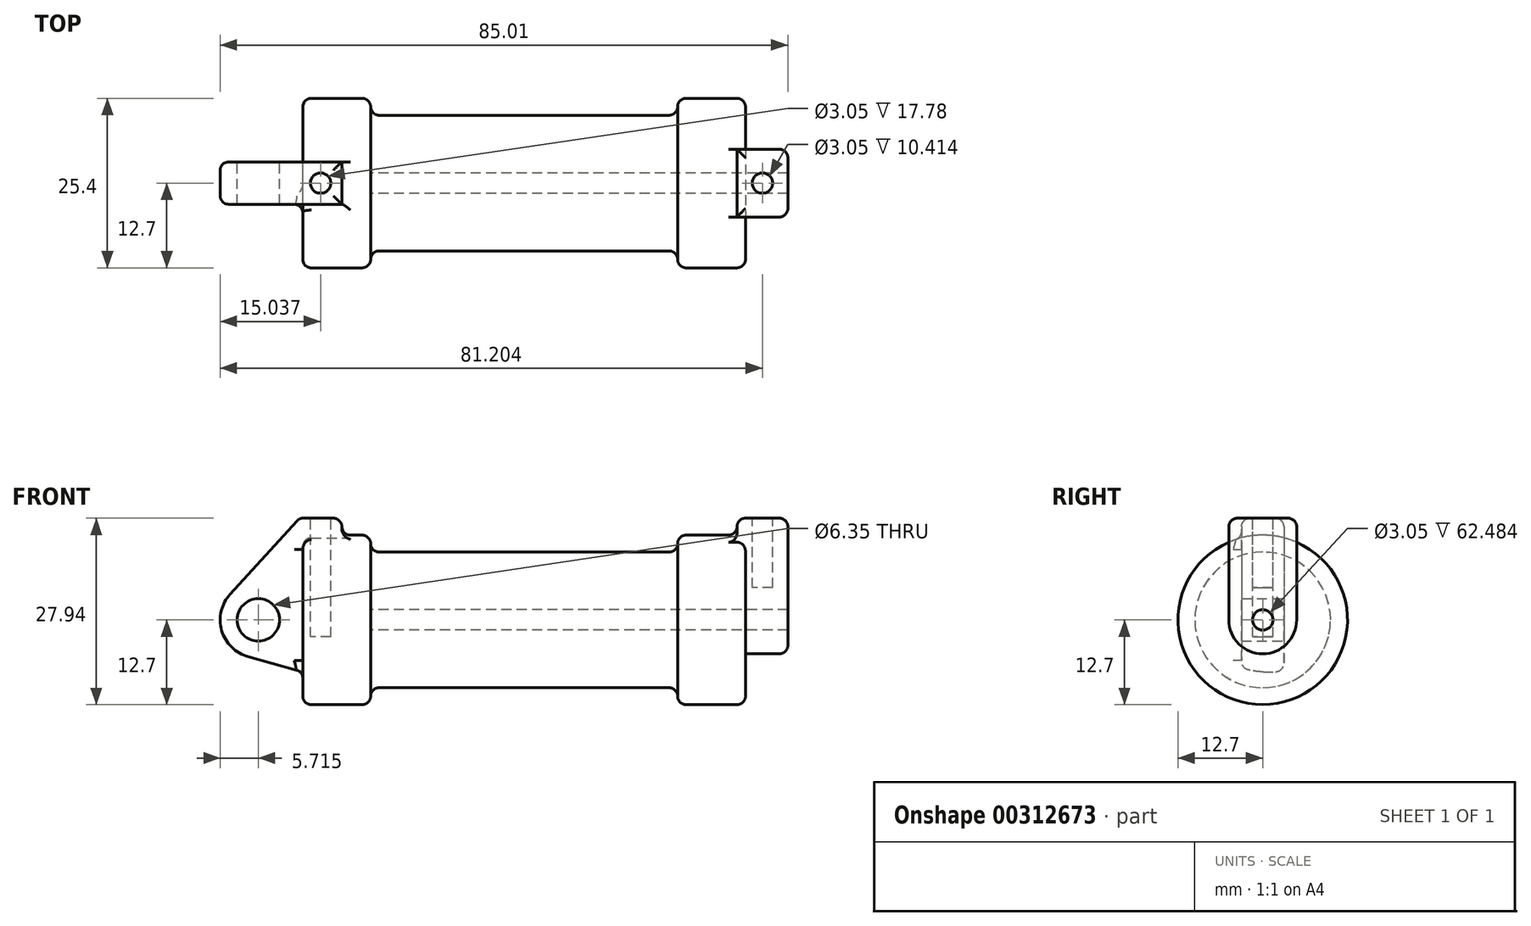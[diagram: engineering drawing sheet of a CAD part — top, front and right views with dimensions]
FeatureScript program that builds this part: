
annotation { "Feature Type Name" : "Feature", "Feature Type Description" : "" }
export const myFeature = defineFeature(function(context is Context, id is Id, definition is map)
    precondition{}
    {
        {
            var Q0;
            Q0=qCreatedBy(makeId("Front.planeOp"),FACE);
            var sketch = newSketch(context, id + "F0", { "sketchPlane" : qUnion([Q0])});
            skLineSegment(sketch, "E0", {"start": v(0, 0) * mm, "end": v(0, 12.7) * mm});
            skLineSegment(sketch, "E1", {"start": v(0, 12.7) * mm, "end": v(10.16, 12.7) * mm});
            skLineSegment(sketch, "E2", {"start": v(10.16, 12.7) * mm, "end": v(10.16, 10.16) * mm});
            skLineSegment(sketch, "E3", {"start": v(10.16, 10.16) * mm, "end": v(56.13, 10.16) * mm});
            skLineSegment(sketch, "E4", {"start": v(56.13, 10.16) * mm, "end": v(56.13, 12.7) * mm});
            skLineSegment(sketch, "E5", {"start": v(56.13, 12.7) * mm, "end": v(66.3, 12.7) * mm});
            skLineSegment(sketch, "E6", {"start": v(66.3, 12.7) * mm, "end": v(66.3, 0) * mm});
            skLineSegment(sketch, "E7", {"start": v(66.3, 0) * mm, "end": v(0, 0) * mm});
            skLineSegment(sketch, "E8", {"start": v(5.84, 15.24) * mm, "end": v(-0.5, 15.24) * mm});
            skLineSegment(sketch, "E9", {"start": v(-0.5, 15.24) * mm, "end": v(-10.88, 3.85) * mm});
            skLineSegment(sketch, "E10", {"start": v(0, 0) * mm, "end": v(-6.65, 0) * mm});
            skCircle(sketch, "E11", {"center": v(-6.65, 0) * mm, "radius": 5.72 * mm});
            skCircle(sketch, "E12", {"center": v(-6.65, 0) * mm, "radius": 3.18 * mm});
            skLineSegment(sketch, "E13", {"start": v(5.84, 15.24) * mm, "end": v(5.84, -9.4) * mm});
            skLineSegment(sketch, "E14", {"start": v(5.84, -9.4) * mm, "end": v(-8.18, -5.5) * mm});
            skSolve(sketch);
        }
        {
            var Q0;
            {var subQ0=sQuery(id+"F0.wireOp",EDGE,"E2");Q0=makeQuery(id+"F0.imprint","IMPRINT",FACE,{"disambiguationData":[TD([[makeQuery(id+"F0.imprint","IMPRINT",EDGE,{"derivedFrom":subQ0}),-1.0]])]});}
            var Q1;
            {var subQ0=sQuery(id+"F0.wireOp",EDGE,"E0");Q1=makeQuery(id+"F0.imprint","IMPRINT",FACE,{"disambiguationData":[TD([[makeQuery(id+"F0.imprint","IMPRINT",EDGE,{"derivedFrom":subQ0}),-1.0]])]});}
            var Q2;
            Q2=sQuery(id+"F0.wireOp",EDGE,"E7");
            revolve(context, id + "F1", {"entities" : qUnion([Q0, Q1]), "axis" : qUnion([Q2]), "revolveType" : RevolveType.FULL});
        }
        {
            var Q0;
            {var subQ0=sQuery(id+"F0.wireOp",EDGE,"E0");Q0=makeQuery(id+"F0.imprint","IMPRINT",FACE,{"disambiguationData":[TD([[makeQuery(id+"F0.imprint","IMPRINT",EDGE,{"derivedFrom":subQ0}),-1.0]])]});}
            var Q1;
            {var subQ1=sQuery(id+"F0.wireOp",EDGE,"E0");Q1=makeQuery(id+"F0.imprint","IMPRINT",FACE,{"disambiguationData":[TD([[makeQuery(id+"F0.imprint","IMPRINT",EDGE,{"derivedFrom":subQ1}),1.0]])]});}
            var Q2;
            {var subQ5=sQuery(id+"F0.wireOp",EDGE,"E12");Q2=makeQuery(id+"F0.imprint","IMPRINT",FACE,{"disambiguationData":[TD([[makeQuery(id+"F0.imprint","IMPRINT",EDGE,{"derivedFrom":subQ5}),-1.0]])]});}
            var Q3;
            {var subQ0=sQuery(id+"F0.wireOp",EDGE,"E14");Q3=makeQuery(id+"F0.imprint","IMPRINT",FACE,{"disambiguationData":[TD([[makeQuery(id+"F0.imprint","IMPRINT",EDGE,{"derivedFrom":subQ0}),-1.0]])]});}
            extrude(context, id + "F2", {"entities" : qUnion([Q0, Q1, Q2, Q3]), "operationType" : NewBodyOperationType.ADD, "endBound" : BoundingType.SYMMETRIC, "depth" : 6.35 * mm});
        }
        {
            var Q0;
            Q0=makeQuery(id+"F1.opRevolve","SWEPT_FACE",FACE,{"disambiguationData":[OSD([sQuery(id+"F0.wireOp",EDGE,"E6")])]});
            var sketch = newSketch(context, id + "F3", { "sketchPlane" : qUnion([Q0])});
            skCircle(sketch, "E15", {"center": v(0, 0) * mm, "radius": 1.52 * mm});
            skCircle(sketch, "E16", {"center": v(0, 0) * mm, "radius": 5.08 * mm});
            skLineSegment(sketch, "E17", {"start": v(5.08, 0) * mm, "end": v(5.08, 15.24) * mm});
            skLineSegment(sketch, "E18", {"start": v(5.08, 15.24) * mm, "end": v(-5.08, 15.24) * mm});
            skLineSegment(sketch, "E19", {"start": v(-5.08, 15.24) * mm, "end": v(-5.08, 0) * mm});
            skSolve(sketch);
        }
        {
            var Q0;
            {var subQ0=sQuery(id+"F3.wireOp",EDGE,"E18");Q0=makeQuery(id+"F3.imprint","IMPRINT",FACE,{"disambiguationData":[TD([[makeQuery(id+"F3.imprint","IMPRINT",EDGE,{"derivedFrom":subQ0}),1.0]])]});}
            var Q1;
            {var subQ0=sQuery(id+"F3.wireOp",EDGE,"E17");var subQ1=sQuery(id+"F3.wireOp",EDGE,"E16");var subQ2=makeQuery(id+"F3.imprint","INTERSECT",VERTEX,{"derivedFrom":[subQ1,subQ0]});Q1=makeQuery(id+"F3.imprint","IMPRINT",FACE,{"disambiguationData":[TD([[makeQuery(id+"F3.imprint","IMPRINT",EDGE,{"disambiguationData":[TD([[subQ2,-1.0]])],"derivedFrom":subQ1}),-1.0]])]});}
            var Q2;
            Q2=makeQuery(id+"F3.imprint","IMPRINT",FACE,{"disambiguationData":[TD([[makeQuery(id+"F3.imprint","IMPRINT",EDGE,{"derivedFrom":sQuery(id+"F3.wireOp",EDGE,"E15")}),-1.0]])]});
            extrude(context, id + "F4", {"entities" : qUnion([Q0, Q1, Q2]), "operationType" : NewBodyOperationType.ADD, "depth" : 6.35 * mm});
        }
        {
            var Q0;
            {var subQ0=sQuery(id+"F3.wireOp",EDGE,"E18");Q0=makeQuery(id+"F3.imprint","IMPRINT",FACE,{"disambiguationData":[TD([[makeQuery(id+"F3.imprint","IMPRINT",EDGE,{"derivedFrom":subQ0}),1.0]])]});}
            var Q1;
            {var subQ0=sQuery(id+"F3.wireOp",EDGE,"E17");var subQ1=sQuery(id+"F3.wireOp",EDGE,"E16");var subQ2=makeQuery(id+"F3.imprint","INTERSECT",VERTEX,{"derivedFrom":[subQ1,subQ0]});Q1=makeQuery(id+"F3.imprint","IMPRINT",FACE,{"disambiguationData":[TD([[makeQuery(id+"F3.imprint","IMPRINT",EDGE,{"disambiguationData":[TD([[subQ2,-1.0]])],"derivedFrom":subQ1}),-1.0]])]});}
            var Q2;
            Q2=makeQuery(id+"F3.imprint","IMPRINT",FACE,{"disambiguationData":[TD([[makeQuery(id+"F3.imprint","IMPRINT",EDGE,{"derivedFrom":sQuery(id+"F3.wireOp",EDGE,"E15")}),-1.0]])]});
            extrude(context, id + "F5", {"entities" : qUnion([Q0, Q1, Q2]), "operationType" : NewBodyOperationType.ADD, "oppositeDirection" : true, "depth" : 1.27 * mm});
        }
        {
            var Q0;
            Q0=makeQuery(id+"F4.boolean.opBoolean","SPLIT",FACE,{"disambiguationData":[TD([makeQuery(id+"F4.opExtrude","SWEPT_FACE",FACE,{"disambiguationData":[OSD([sQuery(id+"F3.wireOp",EDGE,"E15")])]})])],"derivedFrom":makeQuery(id+"F1.opRevolve","SWEPT_FACE",FACE,{"disambiguationData":[OSD([sQuery(id+"F0.wireOp",EDGE,"E6")])]})});
            var Q1;
            Q1=makeQuery(id+"F1.opRevolve","SWEPT_FACE",FACE,{"disambiguationData":[OSD([sQuery(id+"F0.wireOp",EDGE,"E2")])]});
            extrude(context, id + "F6", {"entities" : qUnion([Q0]), "operationType" : NewBodyOperationType.REMOVE, "endBound" : BoundingType.UP_TO_SURFACE, "oppositeDirection" : true, "endBoundEntityFace" : qUnion([Q1]), "depth" : 25.4 * mm});
        }
        {
            var Q0;
            Q0=makeQuery(id+"F2.opExtrude","SWEPT_FACE",FACE,{"disambiguationData":[OSD([sQuery(id+"F0.wireOp",EDGE,"E8")])]});
            var sketch = newSketch(context, id + "F7", { "sketchPlane" : qUnion([Q0])});
            skCircle(sketch, "E20", {"center": v(2.67, 0) * mm, "radius": 1.52 * mm});
            skSolve(sketch);
        }
        {
            var Q0;
            Q0=makeQuery(id+"F7.imprint","IMPRINT",FACE,{"disambiguationData":[TD([[makeQuery(id+"F7.imprint","IMPRINT",EDGE,{"derivedFrom":sQuery(id+"F7.wireOp",EDGE,"E20")}),1.0]])]});
            extrude(context, id + "F8", {"entities" : qUnion([Q0]), "operationType" : NewBodyOperationType.REMOVE, "oppositeDirection" : true, "depth" : 17.78 * mm});
        }
        {
            var Q0;
            {var subQ0=sQuery(id+"F3.wireOp",EDGE,"E18");Q0=makeQuery(id+"F5.boolean.opBoolean","MERGE",FACE,{"derivedFrom":[makeQuery(id+"F4.opExtrude","SWEPT_FACE",FACE,{"disambiguationData":[OSD([subQ0])]}),makeQuery(id+"F5.opExtrude","SWEPT_FACE",FACE,{"disambiguationData":[OSD([subQ0])]})]});}
            var sketch = newSketch(context, id + "F9", { "sketchPlane" : qUnion([Q0])});
            skCircle(sketch, "E21", {"center": v(68.83, 0) * mm, "radius": 1.52 * mm});
            skSolve(sketch);
        }
        {
            var Q0;
            Q0=makeQuery(id+"F9.imprint","IMPRINT",FACE,{"disambiguationData":[TD([[makeQuery(id+"F9.imprint","IMPRINT",EDGE,{"derivedFrom":sQuery(id+"F9.wireOp",EDGE,"E21")}),1.0]])]});
            extrude(context, id + "F10", {"entities" : qUnion([Q0]), "operationType" : NewBodyOperationType.REMOVE, "oppositeDirection" : true, "depth" : 10.4 * mm});
        }
        {
            var Q0;
            Q0=makeQuery(id+"F1.opRevolve","SWEPT_EDGE",EDGE,{"disambiguationData":[OSD([sQuery(id+"F0.wireOp",EDGE,"E2"),sQuery(id+"F0.wireOp",EDGE,"E3")])]});
            var Q1;
            Q1=makeQuery(id+"F1.opRevolve","SWEPT_EDGE",EDGE,{"disambiguationData":[OSD([sQuery(id+"F0.wireOp",EDGE,"E1"),sQuery(id+"F0.wireOp",EDGE,"E2")])]});
            var Q2;
            Q2=makeQuery(id+"F1.opRevolve","SWEPT_EDGE",EDGE,{"disambiguationData":[OSD([sQuery(id+"F0.wireOp",EDGE,"E3"),sQuery(id+"F0.wireOp",EDGE,"E4")])]});
            var Q3;
            Q3=makeQuery(id+"F1.opRevolve","SWEPT_EDGE",EDGE,{"disambiguationData":[OSD([sQuery(id+"F0.wireOp",EDGE,"E4"),sQuery(id+"F0.wireOp",EDGE,"E5")])]});
            fillet(context, id + "F11", {"entities" : qUnion([Q0, Q1, Q2, Q3]), "radius" : 1.27 * mm, "tangentPropagation" : true, "allowEdgeOverflow" : false});
        }
        {
            var Q0;
            Q0=makeQuery(id+"F1.opRevolve","SWEPT_EDGE",EDGE,{"disambiguationData":[OSD([sQuery(id+"F0.wireOp",EDGE,"E0"),sQuery(id+"F0.wireOp",EDGE,"E1")])]});
            fillet(context, id + "F12", {"entities" : qUnion([Q0]), "radius" : 1.27 * mm, "tangentPropagation" : true, "allowEdgeOverflow" : false});
        }
        {
            var Q0;
            {var subQ0=sQuery(id+"F0.wireOp",EDGE,"E5");var subQ1=sQuery(id+"F0.wireOp",EDGE,"E6");Q0=makeQuery(id+"F4.boolean.opBoolean","SPLIT",EDGE,{"disambiguationData":[topologyDisambiguationEdgeConnected([makeQuery(id+"F1.opRevolve","SWEPT_FACE",FACE,{"disambiguationData":[OSD([subQ1])]})])],"derivedFrom":makeQuery(id+"F1.opRevolve","SWEPT_EDGE",EDGE,{"disambiguationData":[OSD([subQ0,subQ1])]})});}
            fillet(context, id + "F13", {"entities" : qUnion([Q0]), "radius" : 1.27 * mm, "tangentPropagation" : true, "allowEdgeOverflow" : false});
        }
        {
            var Q0;
            Q0=makeQuery(id+"F2.opExtrude","SWEPT_EDGE",EDGE,{"disambiguationData":[OSD([sQuery(id+"F0.wireOp",EDGE,"E8"),sQuery(id+"F0.wireOp",EDGE,"E13")])]});
            var Q1;
            Q1=makeQuery(id+"F2.opExtrude","CAP_EDGE",EDGE,{"disambiguationData":[OSD([sQuery(id+"F0.wireOp",EDGE,"E8")])],"isStart":false});
            var Q2;
            Q2=makeQuery(id+"F2.opExtrude","CAP_EDGE",EDGE,{"disambiguationData":[OSD([sQuery(id+"F0.wireOp",EDGE,"E8")])],"isStart":true});
            var Q3;
            Q3=makeQuery(id+"F2.opExtrude","SWEPT_EDGE",EDGE,{"disambiguationData":[OSD([sQuery(id+"F0.wireOp",EDGE,"E8"),sQuery(id+"F0.wireOp",EDGE,"E9")])]});
            var Q4;
            Q4=makeQuery(id+"F2.opExtrude","CAP_EDGE",EDGE,{"disambiguationData":[OSD([sQuery(id+"F0.wireOp",EDGE,"E9")])],"isStart":false});
            var Q5;
            Q5=makeQuery(id+"F2.opExtrude","CAP_EDGE",EDGE,{"disambiguationData":[OSD([sQuery(id+"F0.wireOp",EDGE,"E9")])],"isStart":true});
            var Q6;
            Q6=makeQuery(id+"F2.boolean.opBoolean","INTERSECT",EDGE,{"derivedFrom":[makeQuery(id+"F1.opRevolve","SWEPT_FACE",FACE,{"disambiguationData":[OSD([sQuery(id+"F0.wireOp",EDGE,"E1")])]}),makeQuery(id+"F2.opExtrude","SWEPT_FACE",FACE,{"disambiguationData":[OSD([sQuery(id+"F0.wireOp",EDGE,"E13")])]})]});
            var Q7;
            Q7=makeQuery(id+"F2.boolean.opBoolean","INTERSECT",EDGE,{"derivedFrom":[makeQuery(id+"F1.opRevolve","SWEPT_FACE",FACE,{"disambiguationData":[OSD([sQuery(id+"F0.wireOp",EDGE,"E1")])]}),makeQuery(id+"F2.opExtrude","CAP_FACE",FACE,{"disambiguationData":[OSD([sQuery(id+"F0.wireOp",EDGE,"E8"),sQuery(id+"F0.wireOp",EDGE,"E9"),sQuery(id+"F0.wireOp",EDGE,"E11"),sQuery(id+"F0.wireOp",EDGE,"E12"),sQuery(id+"F0.wireOp",EDGE,"E13"),sQuery(id+"F0.wireOp",EDGE,"E14")])],"isStart":false})]});
            fillet(context, id + "F14", {"entities" : qUnion([Q0, Q1, Q2, Q3, Q4, Q5, Q6, Q7]), "radius" : 1.27 * mm, "tangentPropagation" : true, "allowEdgeOverflow" : false});
        }
        {
            var Q0;
            Q0=makeQuery(id+"F4.opExtrude","CAP_EDGE",EDGE,{"disambiguationData":[OSD([sQuery(id+"F3.wireOp",EDGE,"E18")])],"isStart":false});
            var Q1;
            {var subQ0=sQuery(id+"F3.wireOp",EDGE,"E19");var subQ1=sQuery(id+"F3.wireOp",EDGE,"E18");Q1=makeQuery(id+"F5.boolean.opBoolean","MERGE",EDGE,{"derivedFrom":[makeQuery(id+"F4.opExtrude","SWEPT_EDGE",EDGE,{"disambiguationData":[OSD([subQ1,subQ0])]}),makeQuery(id+"F5.opExtrude","SWEPT_EDGE",EDGE,{"disambiguationData":[OSD([subQ1,subQ0])]})]});}
            var Q2;
            Q2=makeQuery(id+"F5.opExtrude","CAP_EDGE",EDGE,{"disambiguationData":[OSD([sQuery(id+"F3.wireOp",EDGE,"E18")])],"isStart":false});
            var Q3;
            {var subQ0=sQuery(id+"F3.wireOp",EDGE,"E18");var subQ1=sQuery(id+"F3.wireOp",EDGE,"E17");Q3=makeQuery(id+"F5.boolean.opBoolean","MERGE",EDGE,{"derivedFrom":[makeQuery(id+"F4.opExtrude","SWEPT_EDGE",EDGE,{"disambiguationData":[OSD([subQ1,subQ0])]}),makeQuery(id+"F5.opExtrude","SWEPT_EDGE",EDGE,{"disambiguationData":[OSD([subQ1,subQ0])]})]});}
            var Q4;
            Q4=makeQuery(id+"F4.opExtrude","CAP_EDGE",EDGE,{"disambiguationData":[OSD([sQuery(id+"F3.wireOp",EDGE,"E19")])],"isStart":false});
            var Q5;
            {var subQ0=sQuery(id+"F3.wireOp",EDGE,"E19");Q5=makeQuery(id+"F4.boolean.opBoolean","SPLIT",EDGE,{"disambiguationData":[topologyDisambiguationEdgeConnected([makeQuery(id+"F1.opRevolve","SWEPT_FACE",FACE,{"disambiguationData":[OSD([sQuery(id+"F0.wireOp",EDGE,"E6")])]})])],"derivedFrom":makeQuery(id+"F4.opExtrude","CAP_EDGE",EDGE,{"disambiguationData":[OSD([subQ0])],"isStart":true})});}
            var Q6;
            Q6=makeQuery(id+"F5.boolean.opBoolean","INTERSECT",EDGE,{"derivedFrom":[makeQuery(id+"F1.opRevolve","SWEPT_FACE",FACE,{"disambiguationData":[OSD([sQuery(id+"F0.wireOp",EDGE,"E5")])]}),makeQuery(id+"F5.opExtrude","CAP_FACE",FACE,{"disambiguationData":[OSD([sQuery(id+"F3.wireOp",EDGE,"E15"),sQuery(id+"F3.wireOp",EDGE,"E16"),sQuery(id+"F3.wireOp",EDGE,"E17"),sQuery(id+"F3.wireOp",EDGE,"E18"),sQuery(id+"F3.wireOp",EDGE,"E19")])],"isStart":false})]});
            fillet(context, id + "F15", {"entities" : qUnion([Q0, Q1, Q2, Q3, Q4, Q5, Q6]), "radius" : 1.27 * mm, "tangentPropagation" : true, "allowEdgeOverflow" : false});
        }
    });
